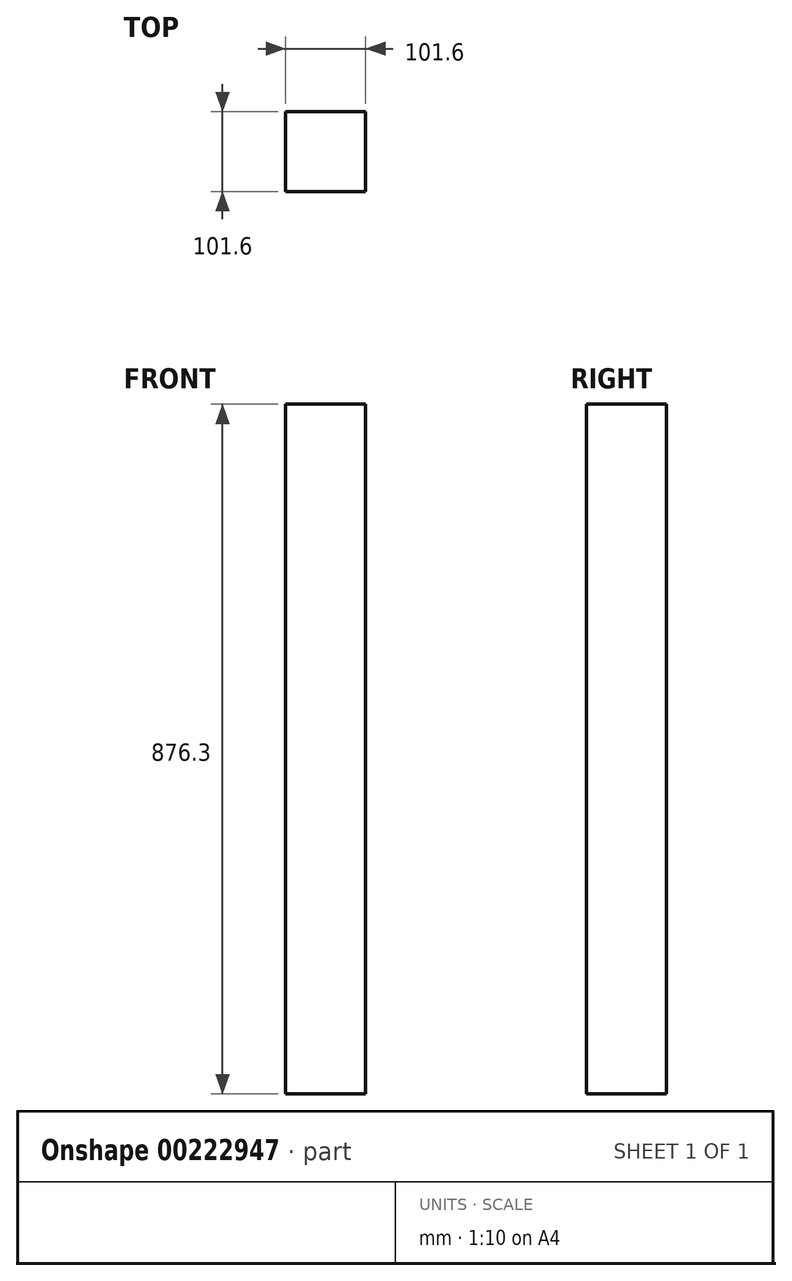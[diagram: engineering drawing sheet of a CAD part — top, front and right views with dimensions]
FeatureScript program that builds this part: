
annotation { "Feature Type Name" : "Feature", "Feature Type Description" : "" }
export const myFeature = defineFeature(function(context is Context, id is Id, definition is map)
    precondition{}
    {
        {
            var Q0;
            Q0=qCreatedBy(makeId("Top.planeOp"),FACE);
            var sketch = newSketch(context, id + "F0", { "sketchPlane" : qUnion([Q0])});
            skLineSegment(sketch, "E0.bottom", {"start": v(0, 0) * mm, "end": v(101.6, 0) * mm});
            skLineSegment(sketch, "E0.top", {"start": v(0, 101.6) * mm, "end": v(101.6, 101.6) * mm});
            skLineSegment(sketch, "E0.left", {"start": v(0, 0) * mm, "end": v(0, 101.6) * mm});
            skLineSegment(sketch, "E0.right", {"start": v(101.6, 0) * mm, "end": v(101.6, 101.6) * mm});
            skSolve(sketch);
        }
        {
            var Q0;
            Q0 = qSketchRegion(id + "F0", true);
            extrude(context, id + "F1", {"entities" : qUnion([Q0]), "depth" : 876.3 * mm});
        }
    });
